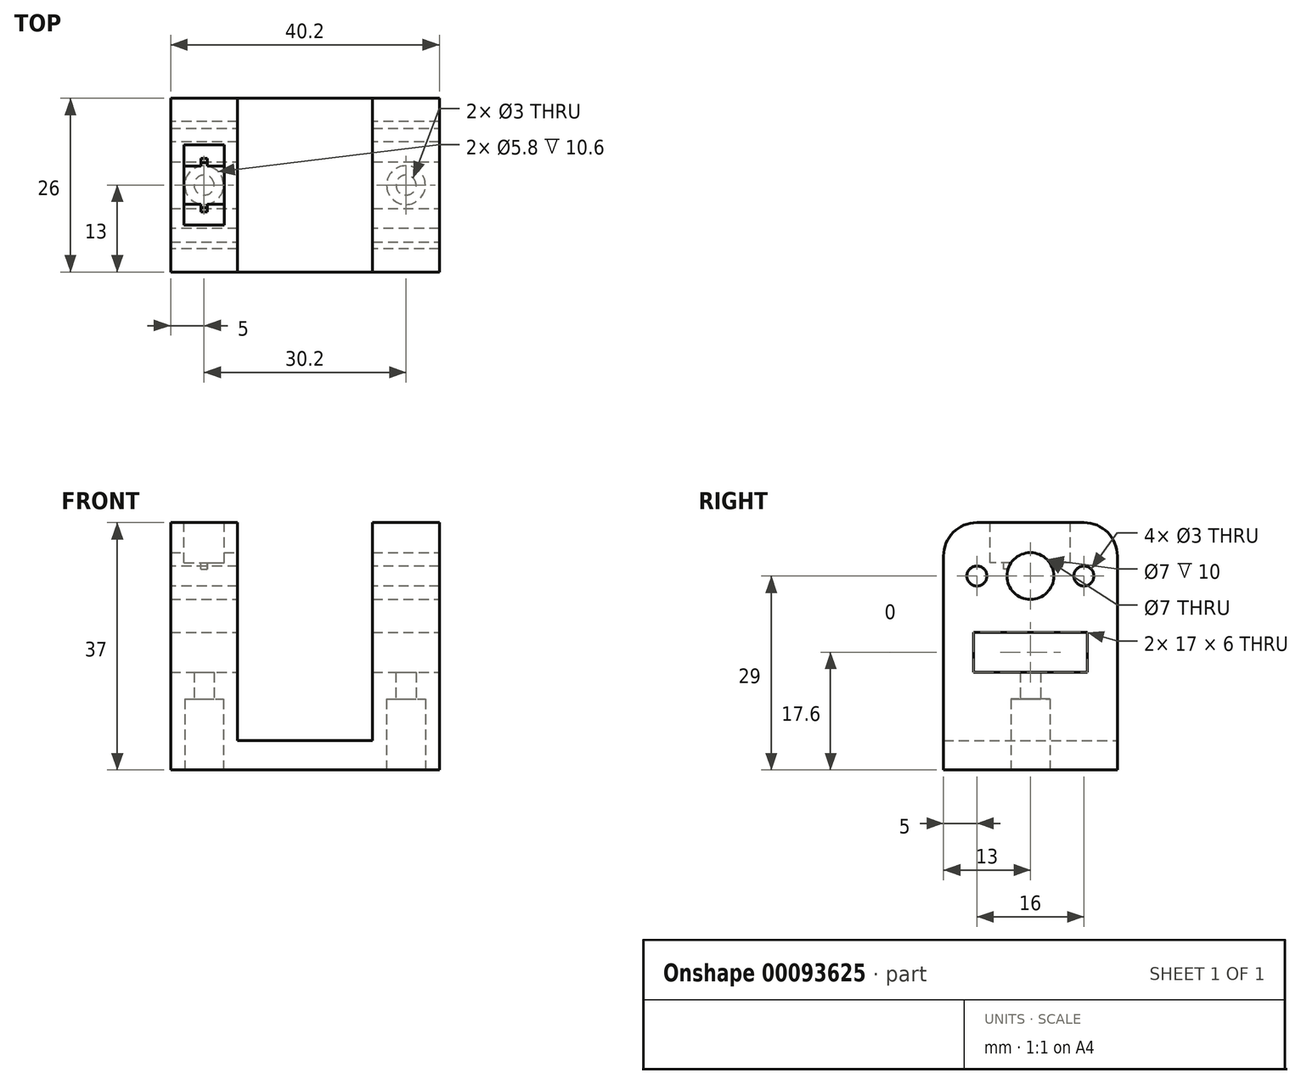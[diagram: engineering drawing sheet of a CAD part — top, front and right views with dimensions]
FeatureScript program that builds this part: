
annotation { "Feature Type Name" : "Feature", "Feature Type Description" : "" }
export const myFeature = defineFeature(function(context is Context, id is Id, definition is map)
    precondition{}
    {
        {
            var Q0;
            Q0=qCreatedBy(makeId("Front.planeOp"),FACE);
            var sketch = newSketch(context, id + "F0", { "sketchPlane" : qUnion([Q0])});
            skLineSegment(sketch, "E0", {"start": v(0, 0) * mm, "end": v(40.2, 0) * mm});
            skLineSegment(sketch, "E1", {"start": v(40.2, 0) * mm, "end": v(40.2, 37) * mm});
            skLineSegment(sketch, "E2", {"start": v(40.2, 37) * mm, "end": v(30.2, 37) * mm});
            skLineSegment(sketch, "E3", {"start": v(30.2, 37) * mm, "end": v(30.2, 4.4) * mm});
            skLineSegment(sketch, "E4", {"start": v(30.2, 4.4) * mm, "end": v(10, 4.4) * mm});
            skLineSegment(sketch, "E5", {"start": v(10, 4.4) * mm, "end": v(10, 37) * mm});
            skLineSegment(sketch, "E6", {"start": v(10, 37) * mm, "end": v(0, 37) * mm});
            skLineSegment(sketch, "E7", {"start": v(0, 37) * mm, "end": v(0, 0) * mm});
            skLineSegment(sketch, "E8", {"start": v(0, 32) * mm, "end": v(40.2, 32) * mm, "construction": true});
            skLineSegment(sketch, "E9", {"start": v(0, 26) * mm, "end": v(40.2, 26) * mm, "construction": true});
            skSolve(sketch);
        }
        {
            var Q0;
            Q0 = qSketchRegion(id + "F0", true);
            extrude(context, id + "F1", {"entities" : qUnion([Q0]), "depth" : 26 * mm});
        }
        {
            var Q0;
            Q0=makeQuery(id+"F1.opExtrude","SWEPT_FACE",FACE,{"disambiguationData":[OSD([sQuery(id+"F0.wireOp",EDGE,"E1")])]});
            var sketch = newSketch(context, id + "F2", { "sketchPlane" : qUnion([Q0])});
            skLineSegment(sketch, "E10.0", {"start": v(-26, 4.4) * mm, "end": v(0, 4.4) * mm, "construction": true});
            skLineSegment(sketch, "E11.bottom", {"start": v(-21.5, 14.6) * mm, "end": v(-4.5, 14.6) * mm});
            skLineSegment(sketch, "E11.top", {"start": v(-21.5, 20.6) * mm, "end": v(-4.5, 20.6) * mm});
            skLineSegment(sketch, "E11.left", {"start": v(-21.5, 14.6) * mm, "end": v(-21.5, 20.6) * mm});
            skLineSegment(sketch, "E11.right", {"start": v(-4.5, 14.6) * mm, "end": v(-4.5, 20.6) * mm});
            skLineSegment(sketch, "E12", {"start": v(-13, 37) * mm, "end": v(-13, 20.6) * mm, "construction": true});
            skSolve(sketch);
        }
        {
            var Q0;
            Q0 = qSketchRegion(id + "F2", true);
            var Q1;
            Q1=makeQuery(id+"F1.opExtrude","SWEPT_FACE",FACE,{"disambiguationData":[OSD([sQuery(id+"F0.wireOp",EDGE,"E7")])]});
            extrude(context, id + "F3", {"entities" : qUnion([Q0]), "operationType" : NewBodyOperationType.REMOVE, "endBound" : BoundingType.UP_TO_SURFACE, "oppositeDirection" : true, "endBoundEntityFace" : qUnion([Q1]), "depth" : 25 * mm});
        }
        {
            var Q0;
            Q0=makeQuery(id+"F1.opExtrude","SWEPT_FACE",FACE,{"disambiguationData":[OSD([sQuery(id+"F0.wireOp",EDGE,"E1")])]});
            var sketch = newSketch(context, id + "F4", { "sketchPlane" : qUnion([Q0])});
            skLineSegment(sketch, "E13.0", {"start": v(-26, 4.4) * mm, "end": v(0, 4.4) * mm, "construction": true});
            skLineSegment(sketch, "E14", {"start": v(-13, 4.4) * mm, "end": v(-13, 29) * mm, "construction": true});
            skPoint(sketch, "E14.endSnap0", {"position": v(-13, 14.6) * mm});
            skCircle(sketch, "E15", {"center": v(-13, 29) * mm, "radius": 3.5 * mm});
            skSolve(sketch);
        }
        {
            var Q0;
            Q0 = qSketchRegion(id + "F4", true);
            var Q1;
            Q1=makeQuery(id+"F1.opExtrude","SWEPT_FACE",FACE,{"disambiguationData":[OSD([sQuery(id+"F0.wireOp",EDGE,"E7")])]});
            extrude(context, id + "F5", {"entities" : qUnion([Q0]), "operationType" : NewBodyOperationType.REMOVE, "endBound" : BoundingType.UP_TO_SURFACE, "oppositeDirection" : true, "endBoundEntityFace" : qUnion([Q1]), "depth" : 25 * mm});
        }
        {
            var Q0;
            Q0=makeQuery(id+"F1.opExtrude","SWEPT_FACE",FACE,{"disambiguationData":[OSD([sQuery(id+"F0.wireOp",EDGE,"E0")])]});
            var sketch = newSketch(context, id + "F6", { "sketchPlane" : qUnion([Q0])});
            skLineSegment(sketch, "E16", {"start": v(40.2, 13) * mm, "end": v(0, 13) * mm, "construction": true});
            skCircle(sketch, "E17", {"center": v(5, 13) * mm, "radius": 1.5 * mm});
            skCircle(sketch, "E18", {"center": v(35.2, 13) * mm, "radius": 1.5 * mm});
            skSolve(sketch);
        }
        {
            var Q0;
            Q0 = qSketchRegion(id + "F6", true);
            var Q1;
            Q1=makeQuery(id+"F3.boolean.opBoolean","COPY",FACE,{"disambiguationData":[TD([makeQuery(id+"F1.opExtrude","SWEPT_FACE",FACE,{"disambiguationData":[OSD([sQuery(id+"F0.wireOp",EDGE,"E1")])]})])],"derivedFrom":makeQuery(id+"F3.opExtrude","SWEPT_FACE",FACE,{"disambiguationData":[OSD([sQuery(id+"F2.wireOp",EDGE,"E11.top")])]})});
            extrude(context, id + "F7", {"entities" : qUnion([Q0]), "operationType" : NewBodyOperationType.REMOVE, "endBound" : BoundingType.UP_TO_SURFACE, "oppositeDirection" : true, "endBoundEntityFace" : qUnion([Q1]), "depth" : 25 * mm});
        }
        {
            var Q0;
            Q0=makeQuery(id+"F1.opExtrude","SWEPT_FACE",FACE,{"disambiguationData":[OSD([sQuery(id+"F0.wireOp",EDGE,"E0")])]});
            var sketch = newSketch(context, id + "F8", { "sketchPlane" : qUnion([Q0])});
            skCircle(sketch, "E19", {"center": v(5, 13) * mm, "radius": 2.9 * mm});
            skCircle(sketch, "E20", {"center": v(35.2, 13) * mm, "radius": 2.9 * mm});
            skSolve(sketch);
        }
        {
            var Q0;
            Q0 = qSketchRegion(id + "F8", true);
            extrude(context, id + "F9", {"entities" : qUnion([Q0]), "operationType" : NewBodyOperationType.REMOVE, "oppositeDirection" : true, "depth" : 10.6 * mm});
        }
        {
            var Q0;
            Q0=makeQuery(id+"F1.opExtrude","SWEPT_FACE",FACE,{"disambiguationData":[OSD([sQuery(id+"F0.wireOp",EDGE,"E7")])]});
            var sketch = newSketch(context, id + "F10", { "sketchPlane" : qUnion([Q0])});
            skLineSegment(sketch, "E21", {"start": v(13, 29) * mm, "end": v(26, 29) * mm, "construction": true});
            skLineSegment(sketch, "E22", {"start": v(13, 29) * mm, "end": v(0, 29) * mm, "construction": true});
            skCircle(sketch, "E23", {"center": v(5, 29) * mm, "radius": 1.5 * mm});
            skCircle(sketch, "E24", {"center": v(21, 29) * mm, "radius": 1.5 * mm});
            skSolve(sketch);
        }
        {
            var Q0;
            Q0 = qSketchRegion(id + "F10", true);
            var Q1;
            Q1=makeQuery(id+"F1.opExtrude","SWEPT_FACE",FACE,{"disambiguationData":[OSD([sQuery(id+"F0.wireOp",EDGE,"E1")])]});
            extrude(context, id + "F11", {"entities" : qUnion([Q0]), "operationType" : NewBodyOperationType.REMOVE, "endBound" : BoundingType.UP_TO_SURFACE, "oppositeDirection" : true, "endBoundEntityFace" : qUnion([Q1]), "depth" : 25 * mm});
        }
        {
            var Q0;
            Q0=makeQuery(id+"F1.opExtrude","SWEPT_FACE",FACE,{"disambiguationData":[OSD([sQuery(id+"F0.wireOp",EDGE,"E6")])]});
            var sketch = newSketch(context, id + "F12", { "sketchPlane" : qUnion([Q0])});
            skLineSegment(sketch, "E25", {"start": v(5, 0) * mm, "end": v(5, -26) * mm, "construction": true});
            skLineSegment(sketch, "E26.bottom", {"start": v(2, -7) * mm, "end": v(8, -7) * mm});
            skLineSegment(sketch, "E26.top", {"start": v(2, -19) * mm, "end": v(8, -19) * mm});
            skLineSegment(sketch, "E26.left", {"start": v(2, -7) * mm, "end": v(2, -19) * mm});
            skLineSegment(sketch, "E26.right", {"start": v(8, -7) * mm, "end": v(8, -19) * mm});
            skPoint(sketch, "E26.middle", {"position": v(5, -13) * mm});
            skSolve(sketch);
        }
        {
            var Q0;
            Q0 = qSketchRegion(id + "F12", true);
            extrude(context, id + "F13", {"entities" : qUnion([Q0]), "operationType" : NewBodyOperationType.REMOVE, "oppositeDirection" : true, "depth" : 6 * mm});
        }
        {
            var Q0;
            {var subQ0=sQuery(id+"F12.wireOp",EDGE,"E26.right");var subQ1=sQuery(id+"F12.wireOp",EDGE,"E26.bottom");var subQ2=sQuery(id+"F12.wireOp",EDGE,"E26.left");Q0=makeQuery(id+"F13.boolean.opBoolean","COPY",FACE,{"disambiguationData":[TD([makeQuery(id+"F13.opExtrude","SWEPT_FACE",FACE,{"disambiguationData":[OSD([subQ1])]})])],"derivedFrom":makeQuery(id+"F13.opExtrude","CAP_FACE",FACE,{"disambiguationData":[OSD([subQ1,sQuery(id+"F12.wireOp",EDGE,"E26.top"),subQ2,subQ0])],"isStart":false})});}
            var sketch = newSketch(context, id + "F14", { "sketchPlane" : qUnion([Q0])});
            skLineSegment(sketch, "E27", {"start": v(5, -7) * mm, "end": v(5, -19) * mm, "construction": true});
            skLineSegment(sketch, "E28.bottom", {"start": v(4.5, -9) * mm, "end": v(5.5, -9) * mm});
            skLineSegment(sketch, "E28.top", {"start": v(4.5, -17) * mm, "end": v(5.5, -17) * mm});
            skLineSegment(sketch, "E28.left", {"start": v(4.5, -9) * mm, "end": v(4.5, -17) * mm});
            skLineSegment(sketch, "E28.right", {"start": v(5.5, -9) * mm, "end": v(5.5, -17) * mm});
            skPoint(sketch, "E28.middle", {"position": v(5, -13) * mm});
            skSolve(sketch);
        }
        {
            var Q0;
            Q0 = qSketchRegion(id + "F14", true);
            extrude(context, id + "F15", {"entities" : qUnion([Q0]), "operationType" : NewBodyOperationType.REMOVE, "oppositeDirection" : true, "depth" : 1 * mm});
        }
        {
            var Q0;
            Q0=makeQuery(id+"F1.opExtrude","CAP_EDGE",EDGE,{"disambiguationData":[OSD([sQuery(id+"F0.wireOp",EDGE,"E6")])],"isStart":false});
            var Q1;
            Q1=makeQuery(id+"F1.opExtrude","CAP_EDGE",EDGE,{"disambiguationData":[OSD([sQuery(id+"F0.wireOp",EDGE,"E6")])],"isStart":true});
            var Q2;
            Q2=makeQuery(id+"F1.opExtrude","CAP_EDGE",EDGE,{"disambiguationData":[OSD([sQuery(id+"F0.wireOp",EDGE,"E2")])],"isStart":true});
            var Q3;
            Q3=makeQuery(id+"F1.opExtrude","CAP_EDGE",EDGE,{"disambiguationData":[OSD([sQuery(id+"F0.wireOp",EDGE,"E2")])],"isStart":false});
            fillet(context, id + "F16", {"entities" : qUnion([Q0, Q1, Q2, Q3]), "radius" : 5 * mm, "tangentPropagation" : true, "allowEdgeOverflow" : false});
        }
    });
